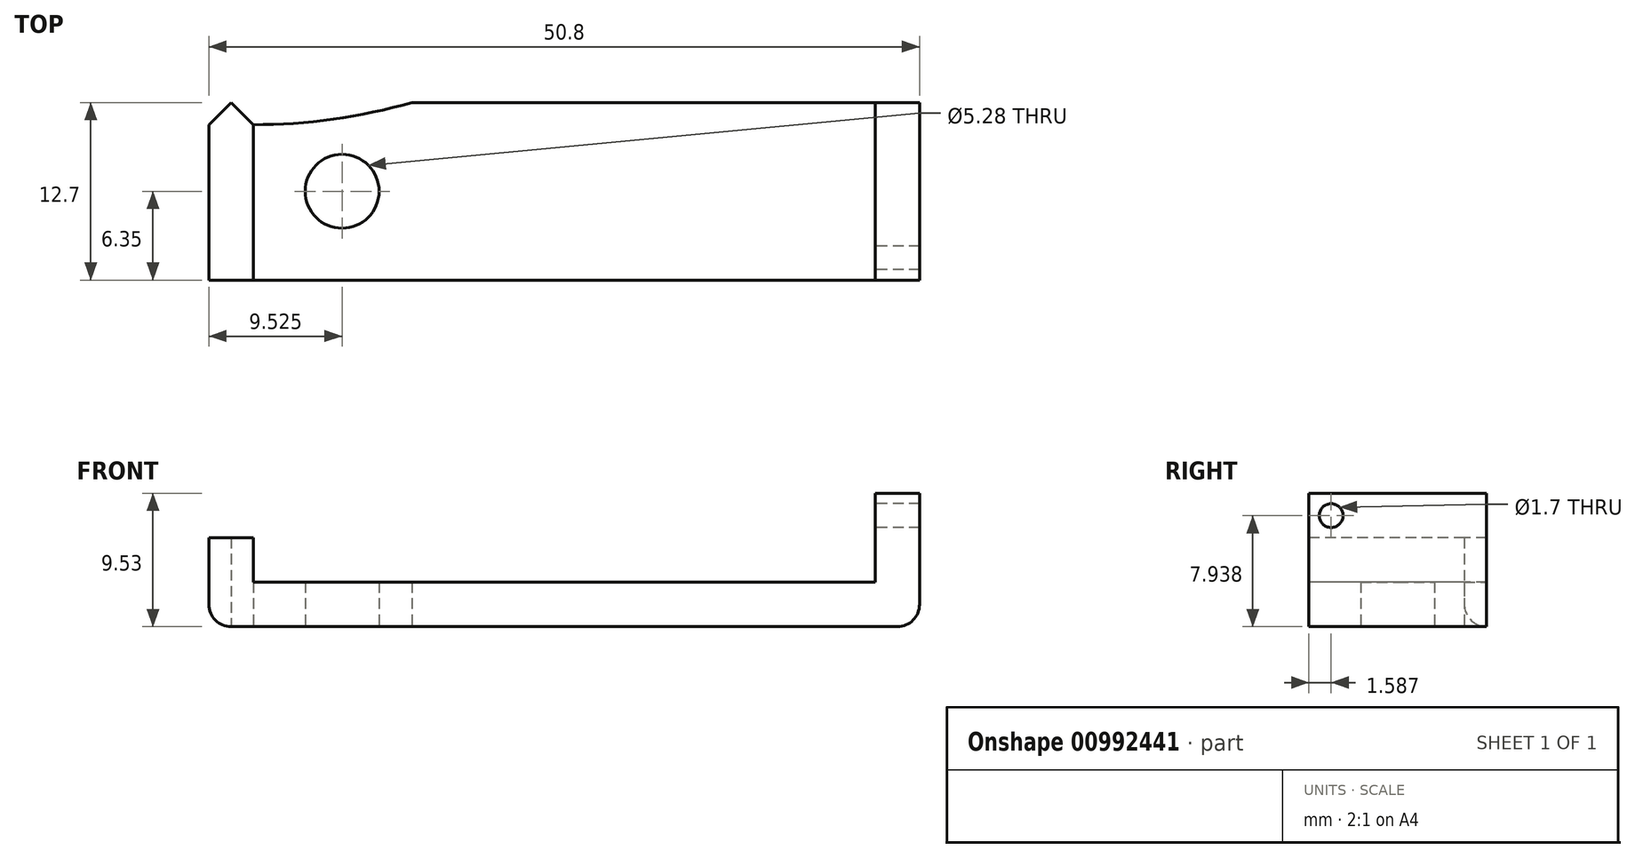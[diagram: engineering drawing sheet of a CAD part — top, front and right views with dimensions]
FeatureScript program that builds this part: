
annotation { "Feature Type Name" : "Feature", "Feature Type Description" : "" }
export const myFeature = defineFeature(function(context is Context, id is Id, definition is map)
    precondition{}
    {
        {
            var Q0;
            Q0=qCreatedBy(makeId("Top.planeOp"),FACE);
            var sketch = newSketch(context, id + "F0", { "sketchPlane" : qUnion([Q0])});
            skLineSegment(sketch, "E0.bottom", {"start": v(25.4, 6.35) * mm, "end": v(-10.89, 6.35) * mm});
            skLineSegment(sketch, "E0.top", {"start": v(25.4, -6.35) * mm, "end": v(-25.4, -6.35) * mm});
            skLineSegment(sketch, "E0.left", {"start": v(25.4, 6.35) * mm, "end": v(25.4, -6.35) * mm});
            skLineSegment(sketch, "E0.right", {"start": v(-25.4, 4.76) * mm, "end": v(-25.4, -6.35) * mm});
            skPoint(sketch, "E0.middle", {"position": v(0, 0) * mm});
            skLineSegment(sketch, "E1.top", {"start": v(-25.4, -6.35) * mm, "end": v(-22.23, -6.35) * mm});
            skLineSegment(sketch, "E1.right", {"start": v(-22.23, 4.76) * mm, "end": v(-22.23, -6.35) * mm});
            skLineSegment(sketch, "E2.bottom", {"start": v(25.4, 6.35) * mm, "end": v(22.22, 6.35) * mm});
            skLineSegment(sketch, "E2.top", {"start": v(25.4, -6.35) * mm, "end": v(22.23, -6.35) * mm});
            skLineSegment(sketch, "E2.right", {"start": v(22.22, 6.35) * mm, "end": v(22.23, -6.35) * mm});
            skCircle(sketch, "E3", {"center": v(-15.88, 0) * mm, "radius": 2.64 * mm});
            skArc(sketch, "E4", {"start": v(-22.23, 4.76) * mm, "mid": v(-16.5, 5.16) * mm, "end": v(-10.89, 6.35) * mm});
            skLineSegment(sketch, "E5", {"start": v(-23.81, 6.35) * mm, "end": v(-25.4, 4.76) * mm});
            skLineSegment(sketch, "E6", {"start": v(-23.81, 6.35) * mm, "end": v(-22.22, 4.76) * mm});
            skSolve(sketch);
        }
        {
            var Q0;
            {var subQ1=sQuery(id+"F0.wireOp",EDGE,"E1.right");Q0=makeQuery(id+"F0.imprint","IMPRINT",FACE,{"disambiguationData":[TD([[makeQuery(id+"F0.imprint","IMPRINT",EDGE,{"derivedFrom":subQ1}),1.0]])]});}
            extrude(context, id + "F1", {"entities" : qUnion([Q0]), "depth" : 3.17 * mm, "offsetDistance" : 25.4 * mm});
        }
        {
            var Q0;
            {var subQ1=sQuery(id+"F0.wireOp",EDGE,"E0.right");Q0=makeQuery(id+"F0.imprint","IMPRINT",FACE,{"disambiguationData":[TD([[makeQuery(id+"F0.imprint","IMPRINT",EDGE,{"derivedFrom":subQ1}),1.0]])]});}
            extrude(context, id + "F2", {"entities" : qUnion([Q0]), "operationType" : NewBodyOperationType.ADD, "depth" : 6.35 * mm, "offsetDistance" : 25.4 * mm});
        }
        {
            var Q0;
            {var subQ2=sQuery(id+"F0.wireOp",EDGE,"E0.left");Q0=makeQuery(id+"F0.imprint","IMPRINT",FACE,{"disambiguationData":[TD([[makeQuery(id+"F0.imprint","IMPRINT",EDGE,{"derivedFrom":subQ2}),-1.0]])]});}
            extrude(context, id + "F3", {"entities" : qUnion([Q0]), "operationType" : NewBodyOperationType.ADD, "depth" : 9.52 * mm, "offsetDistance" : 25.4 * mm});
        }
        {
            var Q0;
            Q0=makeQuery(id+"F1.opExtrude","CAP_EDGE",EDGE,{"disambiguationData":[OSD([sQuery(id+"F0.wireOp",EDGE,"E1.right")])],"isStart":false});
            var Q1;
            Q1=makeQuery(id+"F2.opExtrude","CAP_EDGE",EDGE,{"disambiguationData":[OSD([sQuery(id+"F0.wireOp",EDGE,"E0.right")])],"isStart":true});
            var Q2;
            Q2=makeQuery(id+"F3.opExtrude","CAP_EDGE",EDGE,{"disambiguationData":[OSD([sQuery(id+"F0.wireOp",EDGE,"E0.left")])],"isStart":true});
            var Q3;
            Q3=makeQuery(id+"F1.opExtrude","CAP_EDGE",EDGE,{"disambiguationData":[OSD([sQuery(id+"F0.wireOp",EDGE,"E2.right")])],"isStart":false});
            fillet(context, id + "F4", {"entities" : qUnion([Q0, Q1, Q2, Q3]), "radius" : 1.59 * mm, "tangentPropagation" : true, "allowEdgeOverflow" : false});
        }
        {
            var Q0;
            Q0=makeQuery(id+"F3.opExtrude","SWEPT_FACE",FACE,{"disambiguationData":[OSD([sQuery(id+"F0.wireOp",EDGE,"E0.left")])]});
            var sketch = newSketch(context, id + "F5", { "sketchPlane" : qUnion([Q0])});
            skCircle(sketch, "E7", {"center": v(-4.76, 7.94) * mm, "radius": 0.8 * mm});
            skSolve(sketch);
        }
        {
            var Q0;
            Q0=sQuery(id+"F5.wireOp",VERTEX,"E7.center");
            var Q1;
            Q1=makeQuery(id+"F1.opExtrude","SWEPT_BODY",BODY,{"disambiguationData":[OSD([sQuery(id+"F0.wireOp",EDGE,"E0.bottom"),sQuery(id+"F0.wireOp",EDGE,"E0.top"),sQuery(id+"F0.wireOp",EDGE,"E1.right"),sQuery(id+"F0.wireOp",EDGE,"E2.right"),sQuery(id+"F0.wireOp",EDGE,"E3"),sQuery(id+"F0.wireOp",EDGE,"E4")])]});
            hole(context, id + "F6", {"style" : HoleStyle.SIMPLE, "endStyle" : HoleEndStyle.BLIND, "standardTappedOrClearance" : lookupTablePath({ "fit" : "Close (ASME)", "standard" : "ANSI", "size" : "#0", "type" : "Clearance" }), "standardBlindInLast" : lookupTablePath({ "fit" : "Close", "standard" : "ANSI", "engagement" : "75%", "pitch" : "80 tpi", "size" : "#0", "type" : "Clearance & tapped" }), "holeDiameter" : 1.7 * mm, "majorDiameter" : 6.35 * mm, "holeDepth" : 25.4 * mm, "isTappedThrough" : true, "tappedDepth" : 12.7 * mm, "tapClearance" : 3, "locations" : qUnion([Q0]), "scope" : qUnion([Q1]), "startStyle" : HoleStartStyle.SKETCH});
        }
    });
